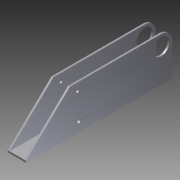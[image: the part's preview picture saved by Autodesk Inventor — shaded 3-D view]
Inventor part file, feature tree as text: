
AUTODESK INVENTOR PART (.ipt)
format: ipt  version: 2012 (Build 160160000, 160)  size: 119,296 bytes
history: native  units: in
note: dims shown in document units (in); Inventor stores cm internally (conversion verified against a paired STEP export)
features: extrude x2, sketch x2
ambient origin geometry x8: Origin, YZ Plane, XZ Plane, XY Plane, X Axis, Y Axis, Z Axis, Center Point
bodies: Solid1 (feature_tree)
feature tree (4):
  extrude  "Extrusion1"  Depth=1.25in
  extrude  "Extrusion2"  Depth=10.0in TaperAngle=0.0deg
  sketch  "Sketch1"  dims[d0=3.0in d1=1.25in]
  sketch  "Sketch2"  dims[d2=0.125in d4=10.0in d5=0.0in d8=3.0in d9=0.5in d13=0.25in d15=1.0in d16=0.0in d17=0.75in d18=1.125in d20=0.125in d21=0.125in d22=1.0in d23=0.5in d24=0.5in d25=0.5in d26=0.25in d27=0.5in]
